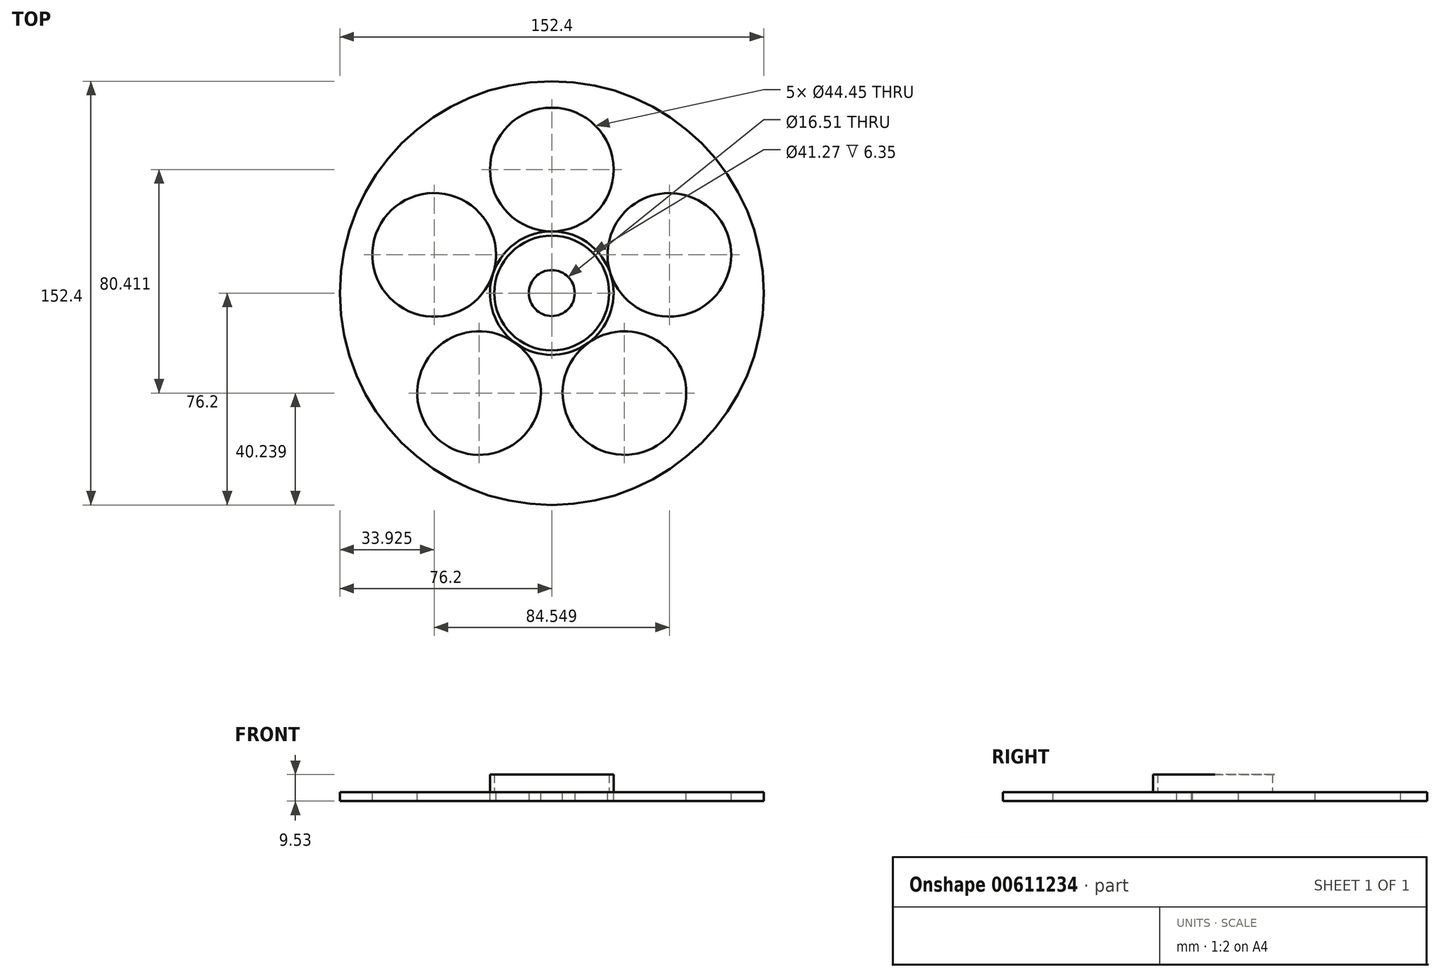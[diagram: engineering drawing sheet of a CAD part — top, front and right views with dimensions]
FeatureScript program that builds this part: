
annotation { "Feature Type Name" : "Feature", "Feature Type Description" : "" }
export const myFeature = defineFeature(function(context is Context, id is Id, definition is map)
    precondition{}
    {
        {
            var Q0;
            Q0=qCreatedBy(makeId("Top.planeOp"),FACE);
            var sketch = newSketch(context, id + "F0", { "sketchPlane" : qUnion([Q0])});
            skCircle(sketch, "E0", {"center": v(0, 0) * mm, "radius": 76.2 * mm});
            skCircle(sketch, "E1", {"center": v(0, 0) * mm, "radius": 8.26 * mm});
            skSolve(sketch);
        }
        {
            var Q0;
            Q0=makeQuery(id+"F0.imprint","IMPRINT",FACE,{"disambiguationData":[TD([[makeQuery(id+"F0.imprint","IMPRINT",EDGE,{"derivedFrom":sQuery(id+"F0.wireOp",EDGE,"E0")}),1.0]])]});
            extrude(context, id + "F1", {"entities" : qUnion([Q0]), "depth" : 3.17 * mm, "offsetDistance" : 25.4 * mm});
        }
        {
            var Q0;
            Q0=makeQuery(id+"F1.opExtrude","CAP_FACE",FACE,{"disambiguationData":[OSD([sQuery(id+"F0.wireOp",EDGE,"E0"),sQuery(id+"F0.wireOp",EDGE,"E1")])],"isStart":false});
            var sketch = newSketch(context, id + "F2", { "sketchPlane" : qUnion([Q0])});
            skCircle(sketch, "E2", {"center": v(0, 44.45) * mm, "radius": 22.23 * mm});
            skCircle(sketch, "E3.1.0", {"center": v(-42.27, 13.74) * mm, "radius": 22.23 * mm});
            skCircle(sketch, "E3.2.0", {"center": v(-26.13, -35.96) * mm, "radius": 22.23 * mm});
            skCircle(sketch, "E3.3.0", {"center": v(26.13, -35.96) * mm, "radius": 22.23 * mm});
            skCircle(sketch, "E3.4.0", {"center": v(42.27, 13.74) * mm, "radius": 22.23 * mm});
            skPoint(sketch, "E3.center", {"position": v(0, 0) * mm});
            skSolve(sketch);
        }
        {
            var Q0;
            Q0=makeQuery(id+"F2.imprint","IMPRINT",FACE,{"disambiguationData":[TD([[makeQuery(id+"F2.imprint","IMPRINT",EDGE,{"derivedFrom":sQuery(id+"F2.wireOp",EDGE,"E2")}),1.0]])]});
            var Q1;
            Q1=makeQuery(id+"F2.imprint","IMPRINT",FACE,{"disambiguationData":[TD([[makeQuery(id+"F2.imprint","IMPRINT",EDGE,{"derivedFrom":sQuery(id+"F2.wireOp",EDGE,"E3.1.0")}),1.0]])]});
            var Q2;
            Q2=makeQuery(id+"F2.imprint","IMPRINT",FACE,{"disambiguationData":[TD([[makeQuery(id+"F2.imprint","IMPRINT",EDGE,{"derivedFrom":sQuery(id+"F2.wireOp",EDGE,"E3.2.0")}),1.0]])]});
            var Q3;
            Q3=makeQuery(id+"F2.imprint","IMPRINT",FACE,{"disambiguationData":[TD([[makeQuery(id+"F2.imprint","IMPRINT",EDGE,{"derivedFrom":sQuery(id+"F2.wireOp",EDGE,"E3.3.0")}),1.0]])]});
            var Q4;
            Q4=makeQuery(id+"F2.imprint","IMPRINT",FACE,{"disambiguationData":[TD([[makeQuery(id+"F2.imprint","IMPRINT",EDGE,{"derivedFrom":sQuery(id+"F2.wireOp",EDGE,"E3.4.0")}),1.0]])]});
            extrude(context, id + "F3", {"entities" : qUnion([Q0, Q1, Q2, Q3, Q4]), "operationType" : NewBodyOperationType.REMOVE, "oppositeDirection" : true, "depth" : 25.4 * mm, "offsetDistance" : 25.4 * mm});
        }
        {
            var Q0;
            Q0=makeQuery(id+"F1.opExtrude","CAP_FACE",FACE,{"disambiguationData":[OSD([sQuery(id+"F0.wireOp",EDGE,"E0"),sQuery(id+"F0.wireOp",EDGE,"E1")])],"isStart":false});
            var sketch = newSketch(context, id + "F4", { "sketchPlane" : qUnion([Q0])});
            skCircle(sketch, "E4", {"center": v(0, 0) * mm, "radius": 22.23 * mm});
            skCircle(sketch, "E5", {"center": v(0, 0) * mm, "radius": 20.64 * mm});
            skSolve(sketch);
        }
        {
            var Q0;
            Q0=makeQuery(id+"F4.imprint","IMPRINT",FACE,{"disambiguationData":[TD([[makeQuery(id+"F4.imprint","IMPRINT",EDGE,{"derivedFrom":sQuery(id+"F4.wireOp",EDGE,"E5")}),-1.0]])]});
            extrude(context, id + "F5", {"entities" : qUnion([Q0]), "operationType" : NewBodyOperationType.ADD, "depth" : 6.35 * mm, "offsetDistance" : 25.4 * mm});
        }
    });
